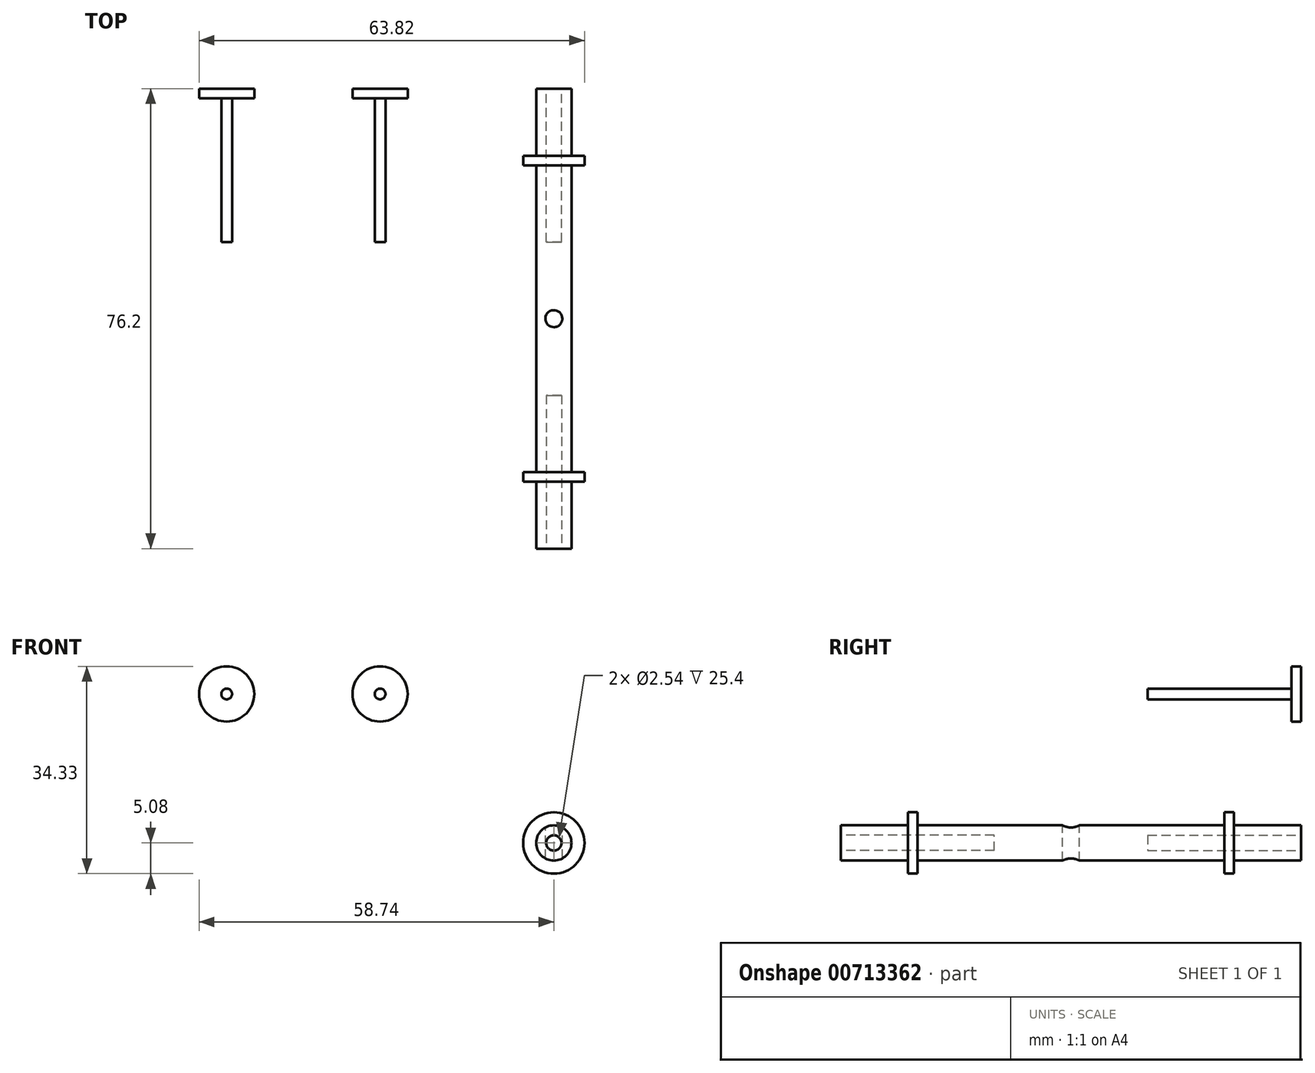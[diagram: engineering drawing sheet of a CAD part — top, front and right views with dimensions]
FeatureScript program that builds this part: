
annotation { "Feature Type Name" : "Feature", "Feature Type Description" : "" }
export const myFeature = defineFeature(function(context is Context, id is Id, definition is map)
    precondition{}
    {
        {
            var Q0;
            Q0=qCreatedBy(makeId("Front.planeOp"),FACE);
            var sketch = newSketch(context, id + "F0", { "sketchPlane" : qUnion([Q0])});
            skCircle(sketch, "E0", {"center": v(0, 0) * mm, "radius": 2.92 * mm});
            skSolve(sketch);
        }
        {
            var Q0;
            Q0 = qSketchRegion(id + "F0", true);
            extrude(context, id + "F1", {"entities" : qUnion([Q0]), "depth" : 76.2 * mm, "offsetDistance" : 25.4 * mm});
        }
        {
            var Q0;
            Q0=makeQuery(id+"F1.opExtrude","CAP_FACE",FACE,{"disambiguationData":[OSD([sQuery(id+"F0.wireOp",EDGE,"E0")])],"isStart":false});
            var sketch = newSketch(context, id + "F2", { "sketchPlane" : qUnion([Q0])});
            skCircle(sketch, "E1", {"center": v(0, 0) * mm, "radius": 1.27 * mm});
            skSolve(sketch);
        }
        {
            var Q0;
            Q0 = qSketchRegion(id + "F2", true);
            extrude(context, id + "F3", {"entities" : qUnion([Q0]), "operationType" : NewBodyOperationType.REMOVE, "depth" : -25.4 * mm, "offsetDistance" : 25.4 * mm});
        }
        {
            var Q0;
            Q0=qCreatedBy(makeId("Front.planeOp"),FACE);
            var sketch = newSketch(context, id + "F4", { "sketchPlane" : qUnion([Q0])});
            skCircle(sketch, "E2", {"center": v(-54.17, 24.67) * mm, "radius": 4.57 * mm});
            skCircle(sketch, "E3", {"center": v(-54.17, 24.67) * mm, "radius": 0.89 * mm});
            skSolve(sketch);
        }
        {
            var Q0;
            Q0 = qSketchRegion(id + "F4", true);
            extrude(context, id + "F5", {"entities" : qUnion([Q0]), "depth" : 1.59 * mm, "offsetDistance" : 25.4 * mm});
        }
        {
            var Q0;
            Q0=makeQuery(id+"F4.imprint","IMPRINT",FACE,{"disambiguationData":[TD([[makeQuery(id+"F4.imprint","IMPRINT",EDGE,{"derivedFrom":sQuery(id+"F4.wireOp",EDGE,"E3")}),1.0]])]});
            extrude(context, id + "F6", {"entities" : qUnion([Q0]), "operationType" : NewBodyOperationType.ADD, "depth" : 25.4 * mm, "offsetDistance" : 25.4 * mm});
        }
        {
            var Q0;
            Q0=makeQuery(id+"F1.opExtrude","CAP_FACE",FACE,{"disambiguationData":[OSD([sQuery(id+"F0.wireOp",EDGE,"E0")])],"isStart":true});
            var sketch = newSketch(context, id + "F7", { "sketchPlane" : qUnion([Q0])});
            skCircle(sketch, "E4", {"center": v(0, 0) * mm, "radius": 1.27 * mm});
            skSolve(sketch);
        }
        {
            var Q0;
            Q0=makeQuery(id+"F7.imprint","IMPRINT",FACE,{"disambiguationData":[TD([[makeQuery(id+"F7.imprint","IMPRINT",EDGE,{"derivedFrom":sQuery(id+"F7.wireOp",EDGE,"E4")}),1.0]])]});
            extrude(context, id + "F8", {"entities" : qUnion([Q0]), "operationType" : NewBodyOperationType.REMOVE, "oppositeDirection" : true, "depth" : 25.4 * mm, "offsetDistance" : 25.4 * mm});
        }
        {
            var Q0;
            Q0=qCreatedBy(makeId("Top.planeOp"),FACE);
            var sketch = newSketch(context, id + "F9", { "sketchPlane" : qUnion([Q0])});
            skLineSegment(sketch, "E5", {"start": v(0, -76.2) * mm, "end": v(0, 0) * mm});
            skPoint(sketch, "E6", {"position": v(0, -38.1) * mm});
            skCircle(sketch, "E7", {"center": v(0, -38.1) * mm, "radius": 1.4 * mm});
            skPoint(sketch, "E8", {"position": v(0, -65.09) * mm});
            skLineSegment(sketch, "E9", {"start": v(-5.08, -65.09) * mm, "end": v(5.08, -65.09) * mm});
            skLineSegment(sketch, "E10", {"start": v(-5.08, -65.09) * mm, "end": v(-5.08, -63.5) * mm});
            skLineSegment(sketch, "E11", {"start": v(5.08, -65.09) * mm, "end": v(5.08, -63.5) * mm});
            skLineSegment(sketch, "E12", {"start": v(-5.08, -63.5) * mm, "end": v(5.08, -63.5) * mm});
            skLineSegment(sketch, "E13.bottom", {"start": v(-1.27, -65.09) * mm, "end": v(1.27, -65.09) * mm});
            skLineSegment(sketch, "E13.top", {"start": v(-1.27, -63.5) * mm, "end": v(1.27, -63.5) * mm});
            skLineSegment(sketch, "E13.left", {"start": v(-1.27, -65.09) * mm, "end": v(-1.27, -63.5) * mm});
            skLineSegment(sketch, "E13.right", {"start": v(1.27, -65.09) * mm, "end": v(1.27, -63.5) * mm});
            skPoint(sketch, "E14", {"position": v(0, -11.11) * mm});
            skLineSegment(sketch, "E15.bottom", {"start": v(0, -11.11) * mm, "end": v(5.08, -11.11) * mm});
            skLineSegment(sketch, "E15.top", {"start": v(0, -12.7) * mm, "end": v(5.08, -12.7) * mm});
            skLineSegment(sketch, "E15.left", {"start": v(0, -11.11) * mm, "end": v(0, -12.7) * mm});
            skLineSegment(sketch, "E15.right", {"start": v(5.08, -11.11) * mm, "end": v(5.08, -12.7) * mm});
            skPoint(sketch, "E16", {"position": v(1.27, -11.11) * mm});
            skLineSegment(sketch, "E17", {"start": v(1.27, -11.11) * mm, "end": v(1.27, -12.7) * mm});
            skSolve(sketch);
        }
        {
            var Q0;
            Q0 = qSketchRegion(id + "F9", true);
            extrude(context, id + "F10", {"entities" : qUnion([Q0]), "operationType" : NewBodyOperationType.REMOVE, "endBound" : BoundingType.SYMMETRIC, "oppositeDirection" : true, "depth" : -25.4 * mm, "offsetDistance" : 25.4 * mm});
        }
        {
            var Q0;
            {var subQ0=sQuery(id+"F9.wireOp",EDGE,"E10");Q0=makeQuery(id+"F9.imprint","IMPRINT",FACE,{"disambiguationData":[TD([[makeQuery(id+"F9.imprint","IMPRINT",EDGE,{"derivedFrom":subQ0}),-1.0]])]});}
            var Q1;
            Q1=sQuery(id+"F9.wireOp",EDGE,"E5");
            revolve(context, id + "F11", {"operationType" : NewBodyOperationType.ADD, "surfaceOperationType" : NewSurfaceOperationType.NEW, "entities" : qUnion([Q0]), "axis" : qUnion([Q1]), "revolveType" : RevolveType.FULL});
        }
        {
            var Q0;
            {var subQ0=sQuery(id+"F9.wireOp",EDGE,"E15.right");Q0=makeQuery(id+"F9.imprint","IMPRINT",FACE,{"disambiguationData":[TD([[makeQuery(id+"F9.imprint","IMPRINT",EDGE,{"derivedFrom":subQ0}),-1.0]])]});}
            var Q1;
            Q1=sQuery(id+"F9.wireOp",EDGE,"E15.left");
            revolve(context, id + "F12", {"operationType" : NewBodyOperationType.ADD, "surfaceOperationType" : NewSurfaceOperationType.NEW, "entities" : qUnion([Q0]), "axis" : qUnion([Q1]), "revolveType" : RevolveType.FULL});
        }
        {
            var Q0;
            Q0=makeQuery(id+"F5.opExtrude","SWEPT_BODY",BODY,{"disambiguationData":[OSD([sQuery(id+"F4.wireOp",EDGE,"E2"),sQuery(id+"F4.wireOp",EDGE,"E3")])]});
            transform(context, id + "F13", {"entities" : qUnion([Q0]), "transformType" : TransformType.TRANSLATION_3D, "dx" : 25.4 * mm, "dy" : 0 * mm, "dz" : 0 * mm, "makeCopy" : true});
        }
    });
